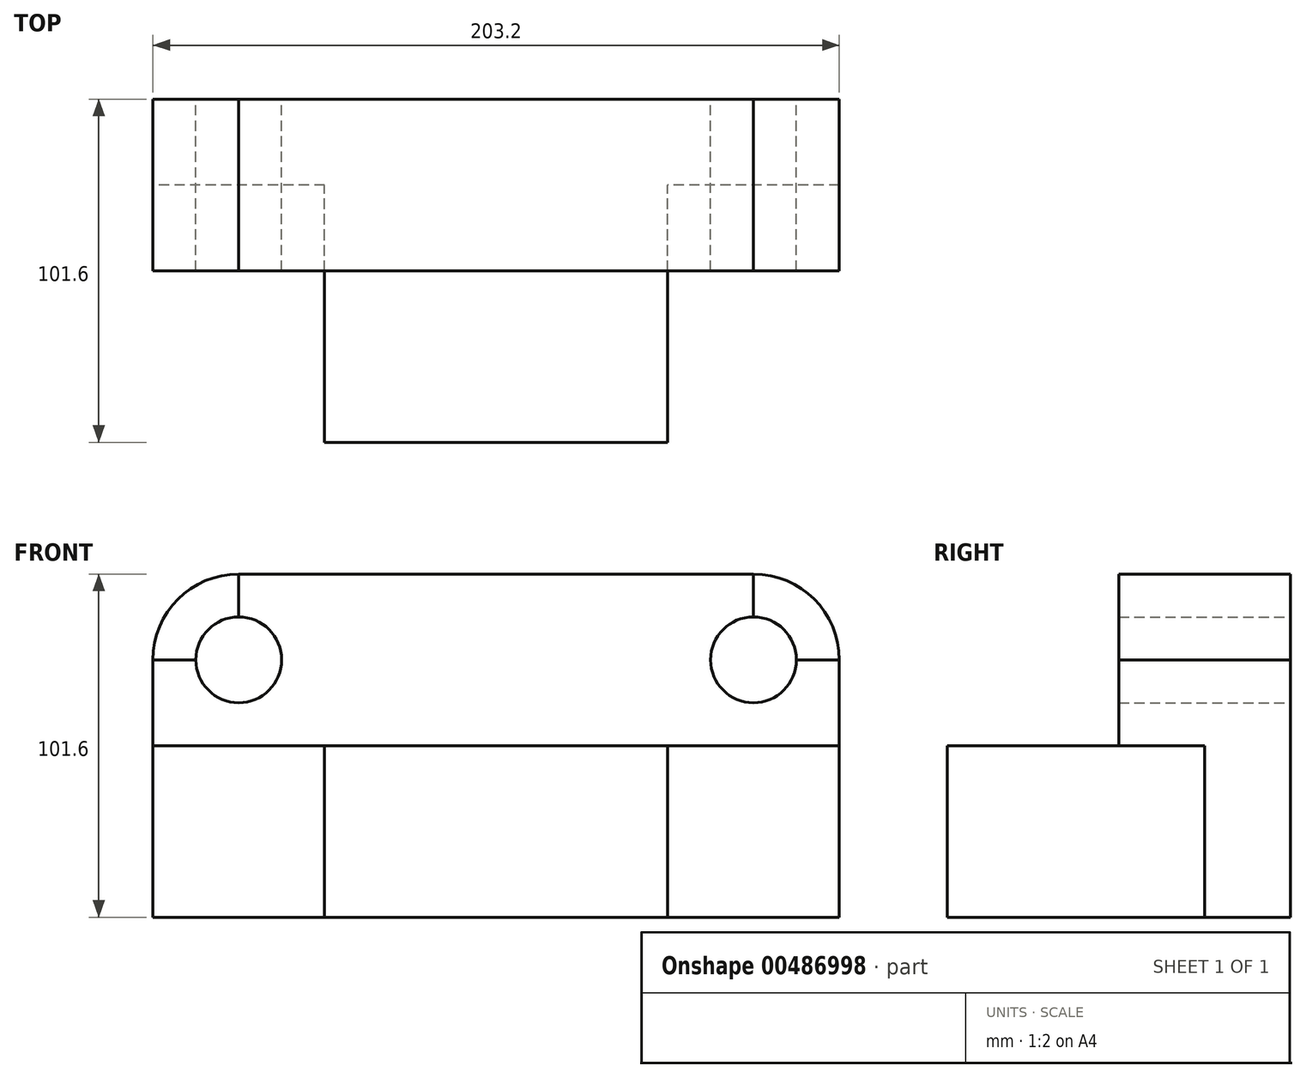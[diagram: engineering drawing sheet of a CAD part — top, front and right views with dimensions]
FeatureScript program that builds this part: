
annotation { "Feature Type Name" : "Feature", "Feature Type Description" : "" }
export const myFeature = defineFeature(function(context is Context, id is Id, definition is map)
    precondition{}
    {
        {
            var Q0;
            Q0=qCreatedBy(makeId("Front.planeOp"),FACE);
            var sketch = newSketch(context, id + "F0", { "sketchPlane" : qUnion([Q0])});
            skLineSegment(sketch, "E0.bottom", {"start": v(0, 0) * mm, "end": v(-50.8, 0) * mm});
            skLineSegment(sketch, "E0.top", {"start": v(0, 50.8) * mm, "end": v(-50.8, 50.8) * mm});
            skLineSegment(sketch, "E0.left", {"start": v(0, 0) * mm, "end": v(0, 50.8) * mm});
            skLineSegment(sketch, "E0.right", {"start": v(-50.8, 0) * mm, "end": v(-50.8, 50.8) * mm});
            skLineSegment(sketch, "E1.bottom", {"start": v(-50.8, 50.8) * mm, "end": v(-152.4, 50.8) * mm});
            skLineSegment(sketch, "E1.top", {"start": v(-50.8, 0) * mm, "end": v(-152.4, 0) * mm});
            skLineSegment(sketch, "E1.left", {"start": v(-50.8, 50.8) * mm, "end": v(-50.8, 0) * mm});
            skLineSegment(sketch, "E1.right", {"start": v(-152.4, 50.8) * mm, "end": v(-152.4, 0) * mm});
            skLineSegment(sketch, "E2.bottom", {"start": v(-152.4, 50.8) * mm, "end": v(-203.2, 50.8) * mm});
            skLineSegment(sketch, "E2.top", {"start": v(-152.4, 0) * mm, "end": v(-203.2, 0) * mm});
            skLineSegment(sketch, "E2.right", {"start": v(-203.2, 50.8) * mm, "end": v(-203.2, 0) * mm});
            skLineSegment(sketch, "E3.bottom", {"start": v(-203.2, 50.8) * mm, "end": v(0, 50.8) * mm});
            skLineSegment(sketch, "E3.top", {"start": v(-203.2, 76.2) * mm, "end": v(-190.5, 76.2) * mm});
            skLineSegment(sketch, "E3.left", {"start": v(-203.2, 50.8) * mm, "end": v(-203.2, 76.2) * mm});
            skLineSegment(sketch, "E3.right", {"start": v(0, 50.8) * mm, "end": v(0, 76.2) * mm});
            skLineSegment(sketch, "E4.top", {"start": v(-203.2, 101.6) * mm, "end": v(-177.8, 101.6) * mm});
            skLineSegment(sketch, "E4.left", {"start": v(-203.2, 76.2) * mm, "end": v(-203.2, 101.6) * mm});
            skLineSegment(sketch, "E4.right", {"start": v(-177.8, 88.9) * mm, "end": v(-177.8, 101.6) * mm});
            skLineSegment(sketch, "E5.bottom", {"start": v(0, 76.2) * mm, "end": v(-12.7, 76.2) * mm});
            skLineSegment(sketch, "E5.top", {"start": v(0, 101.6) * mm, "end": v(-25.4, 101.6) * mm});
            skLineSegment(sketch, "E5.left", {"start": v(0, 76.2) * mm, "end": v(0, 101.6) * mm});
            skLineSegment(sketch, "E5.right", {"start": v(-25.4, 88.9) * mm, "end": v(-25.4, 101.6) * mm});
            skLineSegment(sketch, "E6.bottom", {"start": v(-177.8, 101.6) * mm, "end": v(-25.4, 101.6) * mm});
            skLineSegment(sketch, "E6.left", {"start": v(-177.8, 101.6) * mm, "end": v(-177.8, 88.9) * mm});
            skLineSegment(sketch, "E6.right", {"start": v(-25.4, 101.6) * mm, "end": v(-25.4, 88.9) * mm});
            skCircle(sketch, "E7", {"center": v(-177.8, 76.2) * mm, "radius": 12.7 * mm});
            skCircle(sketch, "E8", {"center": v(-25.4, 76.2) * mm, "radius": 12.7 * mm});
            skLineSegment(sketch, "E9.trimOffspring", {"start": v(-12.7, 76.2) * mm, "end": v(0, 76.2) * mm});
            skSolve(sketch);
        }
        {
            var Q0;
            Q0=makeQuery(id+"F0.imprint","IMPRINT",FACE,{"disambiguationData":[TD([[makeQuery(id+"F0.imprint","IMPRINT",EDGE,{"derivedFrom":sQuery(id+"F0.wireOp",EDGE,"E1.top")}),-1.0]])]});
            extrude(context, id + "F1", {"entities" : qUnion([Q0]), "depth" : 101.6 * mm});
        }
        {
            var Q0;
            Q0=makeQuery(id+"F0.imprint","IMPRINT",FACE,{"disambiguationData":[TD([[makeQuery(id+"F0.imprint","IMPRINT",EDGE,{"derivedFrom":sQuery(id+"F0.wireOp",EDGE,"E2.top")}),-1.0]])]});
            var Q1;
            Q1=makeQuery(id+"F0.imprint","IMPRINT",FACE,{"disambiguationData":[TD([[makeQuery(id+"F0.imprint","IMPRINT",EDGE,{"derivedFrom":sQuery(id+"F0.wireOp",EDGE,"E0.bottom")}),-1.0]])]});
            extrude(context, id + "F2", {"entities" : qUnion([Q0, Q1]), "operationType" : NewBodyOperationType.ADD, "depth" : 25.4 * mm});
        }
        {
            var Q0;
            {var subQ5=sQuery(id+"F0.wireOp",EDGE,"E3.left");Q0=makeQuery(id+"F0.imprint","IMPRINT",FACE,{"disambiguationData":[TD([[makeQuery(id+"F0.imprint","IMPRINT",EDGE,{"derivedFrom":subQ5}),-1.0]])]});}
            extrude(context, id + "F3", {"entities" : qUnion([Q0]), "operationType" : NewBodyOperationType.ADD, "depth" : 50.8 * mm});
        }
        {
            var Q0;
            Q0=makeQuery(id+"F0.imprint","IMPRINT",FACE,{"disambiguationData":[TD([[makeQuery(id+"F0.imprint","IMPRINT",EDGE,{"derivedFrom":sQuery(id+"F0.wireOp",EDGE,"E5.top")}),1.0]])]});
            var Q1;
            {var subQ1=sQuery(id+"F0.wireOp",EDGE,"E3.top");Q1=makeQuery(id+"F0.imprint","IMPRINT",FACE,{"disambiguationData":[TD([[makeQuery(id+"F0.imprint","IMPRINT",EDGE,{"derivedFrom":subQ1}),1.0]])]});}
            extrude(context, id + "F4", {"entities" : qUnion([Q0, Q1]), "depth" : 50.8 * mm});
        }
        {
            var Q0;
            Q0=makeQuery(id+"F4.opExtrude","SWEPT_EDGE",EDGE,{"disambiguationData":[OSD([sQuery(id+"F0.wireOp",EDGE,"E5.top"),sQuery(id+"F0.wireOp",EDGE,"E5.left")])]});
            var Q1;
            Q1=makeQuery(id+"F4.opExtrude","SWEPT_EDGE",EDGE,{"disambiguationData":[OSD([sQuery(id+"F0.wireOp",EDGE,"E4.top"),sQuery(id+"F0.wireOp",EDGE,"E4.left")])]});
            fillet(context, id + "F5", {"entities" : qUnion([Q0, Q1]), "radius" : 25.4 * mm, "tangentPropagation" : true, "allowEdgeOverflow" : false});
        }
    });
